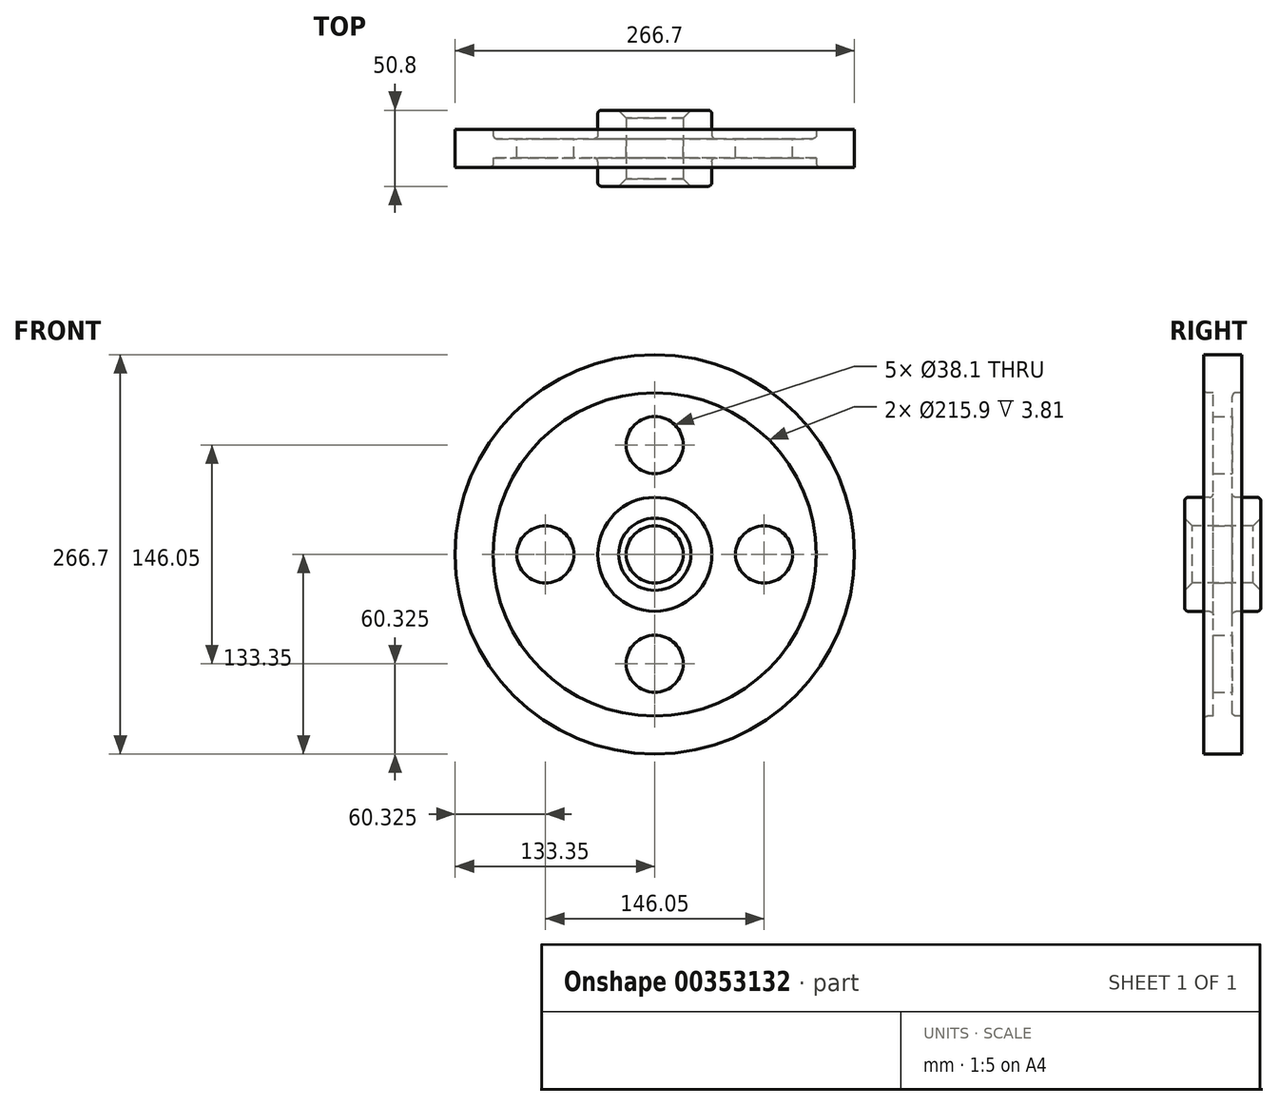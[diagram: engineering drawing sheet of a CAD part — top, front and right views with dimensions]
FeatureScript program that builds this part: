
annotation { "Feature Type Name" : "Feature", "Feature Type Description" : "" }
export const myFeature = defineFeature(function(context is Context, id is Id, definition is map)
    precondition{}
    {
        {
            var Q0;
            Q0=qCreatedBy(makeId("Right.planeOp"),FACE);
            var sketch = newSketch(context, id + "F0", { "sketchPlane" : qUnion([Q0])});
            skLineSegment(sketch, "E0", {"start": v(0, 0) * mm, "end": v(76.2, 0) * mm, "construction": true});
            skLineSegment(sketch, "E1.0", {"start": v(0, 19.05) * mm, "end": v(25.4, 19.05) * mm});
            skLineSegment(sketch, "E2.0", {"start": v(6.35, 38.1) * mm, "end": v(25.4, 38.1) * mm});
            skLineSegment(sketch, "E3.0", {"start": v(6.35, 107.95) * mm, "end": v(12.7, 107.95) * mm});
            skLineSegment(sketch, "E4", {"start": v(0, 0) * mm, "end": v(0, 133.35) * mm, "construction": true});
            skLineSegment(sketch, "E5.trimOffspring", {"start": v(12.7, 107.95) * mm, "end": v(12.7, 133.35) * mm});
            skLineSegment(sketch, "E6.trimOffspring", {"start": v(6.35, 38.1) * mm, "end": v(6.35, 107.95) * mm});
            skLineSegment(sketch, "E7.0", {"start": v(25.4, 19.05) * mm, "end": v(25.4, 38.1) * mm});
            skLineSegment(sketch, "E8.MirrorCS", {"start": v(-6.35, 133.35) * mm, "end": v(-12.7, 133.35) * mm});
            skLineSegment(sketch, "E9.MirrorCS", {"start": v(0, 133.35) * mm, "end": v(-6.35, 133.35) * mm});
            skLineSegment(sketch, "E10.MirrorCS", {"start": v(-12.7, 107.95) * mm, "end": v(-12.7, 133.35) * mm});
            skLineSegment(sketch, "E11.MirrorCS", {"start": v(-6.35, 38.1) * mm, "end": v(-6.35, 107.95) * mm});
            skLineSegment(sketch, "E12.MirrorCS", {"start": v(-6.35, 107.95) * mm, "end": v(-12.7, 107.95) * mm});
            skLineSegment(sketch, "E13.MirrorCS", {"start": v(-6.35, 38.1) * mm, "end": v(-25.4, 38.1) * mm});
            skLineSegment(sketch, "E14.MirrorCS", {"start": v(-25.4, 19.05) * mm, "end": v(-25.4, 38.1) * mm});
            skLineSegment(sketch, "E15.MirrorCS", {"start": v(0, 19.05) * mm, "end": v(-25.4, 19.05) * mm});
            skPoint(sketch, "E16.0.end.orphan", {"position": v(6.35, 133.35) * mm});
            skLineSegment(sketch, "E17", {"start": v(0, 133.35) * mm, "end": v(6.35, 133.35) * mm});
            skLineSegment(sketch, "E18", {"start": v(12.7, 133.35) * mm, "end": v(6.35, 133.35) * mm});
            skSolve(sketch);
        }
        {
            var Q0;
            Q0=makeQuery(id+"F0.imprint","IMPRINT",FACE,{"disambiguationData":[TD([[makeQuery(id+"F0.imprint","IMPRINT",EDGE,{"derivedFrom":sQuery(id+"F0.wireOp",EDGE,"E1.0")}),1.0]])]});
            var Q1;
            Q1=sQuery(id+"F0.wireOp",EDGE,"E0");
            revolve(context, id + "F1", {"entities" : qUnion([Q0]), "axis" : qUnion([Q1]), "revolveType" : RevolveType.FULL});
        }
        {
            var Q0;
            Q0=makeQuery(id+"F1.opRevolve","SWEPT_FACE",FACE,{"disambiguationData":[OSD([sQuery(id+"F0.wireOp",EDGE,"E6.trimOffspring")])]});
            var sketch = newSketch(context, id + "F2", { "sketchPlane" : qUnion([Q0])});
            skLineSegment(sketch, "E19", {"start": v(0, 0) * mm, "end": v(0, 73.03) * mm});
            skCircle(sketch, "E20", {"center": v(0, 73.03) * mm, "radius": 19.05 * mm});
            skCircle(sketch, "E21.1.0", {"center": v(-73.03, 0) * mm, "radius": 19.05 * mm});
            skCircle(sketch, "E21.2.0", {"center": v(0, -73.03) * mm, "radius": 19.05 * mm});
            skCircle(sketch, "E21.3.0", {"center": v(73.03, 0) * mm, "radius": 19.05 * mm});
            skPoint(sketch, "E21.center", {"position": v(0, 0) * mm});
            skSolve(sketch);
        }
        {
            var Q0;
            Q0=makeQuery(id+"F2.imprint","IMPRINT",FACE,{"disambiguationData":[TD([[makeQuery(id+"F2.imprint","IMPRINT",EDGE,{"derivedFrom":sQuery(id+"F2.wireOp",EDGE,"E21.1.0")}),1.0]])]});
            var Q1;
            Q1=makeQuery(id+"F2.imprint","IMPRINT",FACE,{"disambiguationData":[TD([[makeQuery(id+"F2.imprint","IMPRINT",EDGE,{"derivedFrom":sQuery(id+"F2.wireOp",EDGE,"E21.2.0")}),1.0]])]});
            var Q2;
            Q2=makeQuery(id+"F2.imprint","IMPRINT",FACE,{"disambiguationData":[TD([[makeQuery(id+"F2.imprint","IMPRINT",EDGE,{"derivedFrom":sQuery(id+"F2.wireOp",EDGE,"E20")}),1.0]])]});
            var Q3;
            Q3=makeQuery(id+"F2.imprint","IMPRINT",FACE,{"disambiguationData":[TD([[makeQuery(id+"F2.imprint","IMPRINT",EDGE,{"derivedFrom":sQuery(id+"F2.wireOp",EDGE,"E21.3.0")}),1.0]])]});
            extrude(context, id + "F3", {"entities" : qUnion([Q0, Q1, Q2, Q3]), "operationType" : NewBodyOperationType.REMOVE, "oppositeDirection" : true, "depth" : 25.4 * mm});
        }
        {
            var Q0;
            Q0=makeQuery(id+"F1.opRevolve","SWEPT_FACE",FACE,{"disambiguationData":[OSD([sQuery(id+"F0.wireOp",EDGE,"E13.MirrorCS")])]});
            var Q1;
            Q1=makeQuery(id+"F1.opRevolve","SWEPT_EDGE",EDGE,{"disambiguationData":[OSD([sQuery(id+"F0.wireOp",EDGE,"E10.MirrorCS"),sQuery(id+"F0.wireOp",EDGE,"E12.MirrorCS")])]});
            var Q2;
            Q2=makeQuery(id+"F1.opRevolve","SWEPT_FACE",FACE,{"disambiguationData":[OSD([sQuery(id+"F0.wireOp",EDGE,"E2.0")])]});
            var Q3;
            Q3=makeQuery(id+"F1.opRevolve","SWEPT_EDGE",EDGE,{"disambiguationData":[OSD([sQuery(id+"F0.wireOp",EDGE,"E3.0"),sQuery(id+"F0.wireOp",EDGE,"E6.trimOffspring")])]});
            fillet(context, id + "F4", {"entities" : qUnion([Q0, Q1, Q2, Q3]), "radius" : 2.54 * mm, "tangentPropagation" : true, "allowEdgeOverflow" : false});
        }
        {
            var Q0;
            Q0=makeQuery(id+"F1.opRevolve","SWEPT_FACE",FACE,{"disambiguationData":[OSD([sQuery(id+"F0.wireOp",EDGE,"E1.0"),sQuery(id+"F0.wireOp",EDGE,"E15.MirrorCS")])]});
            chamfer(context, id + "F5", {"entities" : qUnion([Q0]), "width" : 5.08 * mm, "tangentPropagation" : true});
        }
    });
